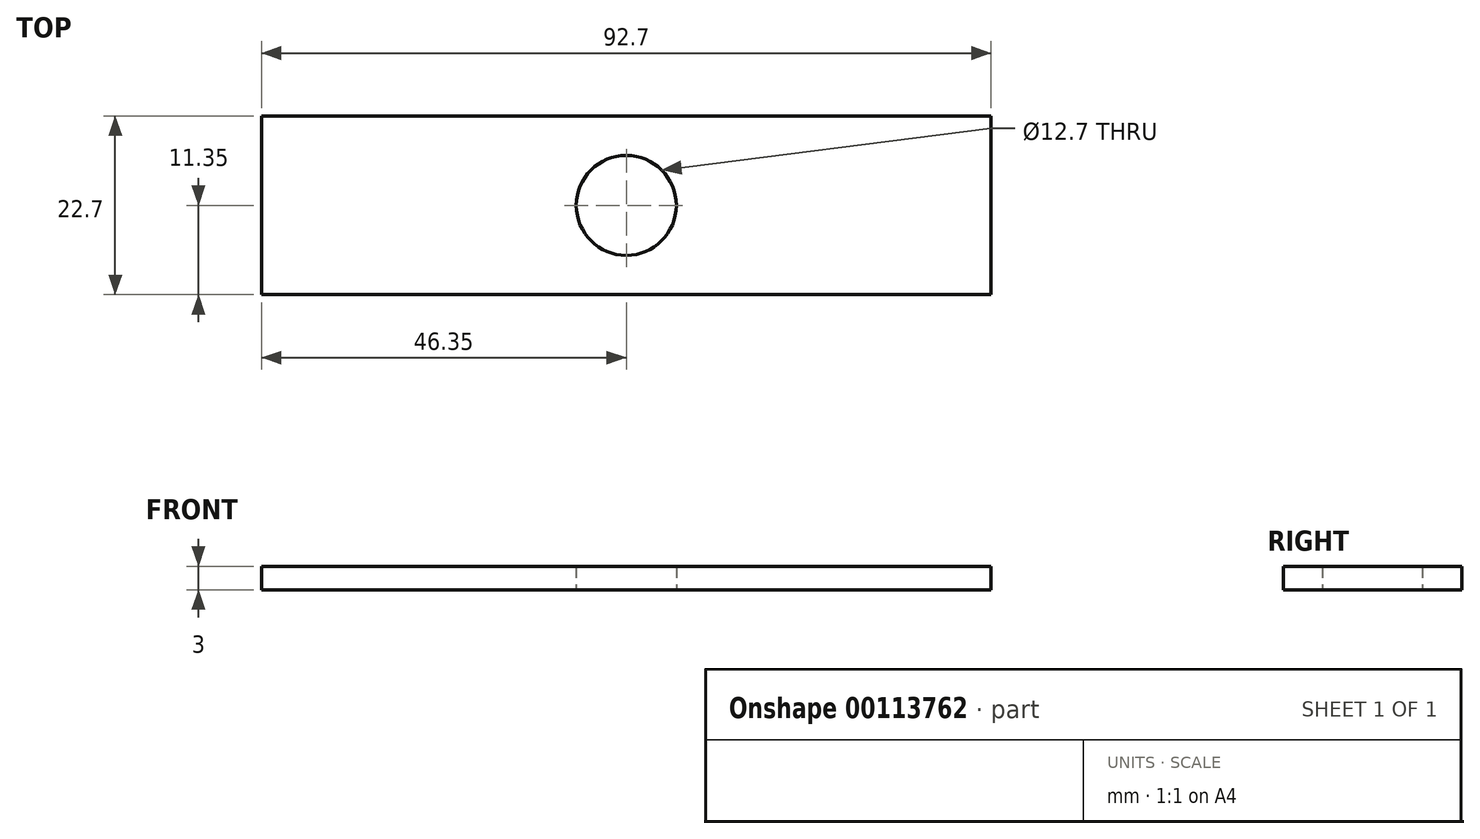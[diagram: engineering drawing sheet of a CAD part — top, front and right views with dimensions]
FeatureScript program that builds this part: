
annotation { "Feature Type Name" : "Feature", "Feature Type Description" : "" }
export const myFeature = defineFeature(function(context is Context, id is Id, definition is map)
    precondition{}
    {
        {
            var Q0;
            Q0=qCreatedBy(makeId("Top.planeOp"),FACE);
            var sketch = newSketch(context, id + "F0", { "sketchPlane" : qUnion([Q0])});
            skLineSegment(sketch, "E0.bottom", {"start": v(46.35, -11.35) * mm, "end": v(-46.35, -11.35) * mm});
            skLineSegment(sketch, "E0.top", {"start": v(46.35, 11.35) * mm, "end": v(-46.35, 11.35) * mm});
            skLineSegment(sketch, "E0.left", {"start": v(46.35, -11.35) * mm, "end": v(46.35, 11.35) * mm});
            skLineSegment(sketch, "E0.right", {"start": v(-46.35, -11.35) * mm, "end": v(-46.35, 11.35) * mm});
            skPoint(sketch, "E0.middle", {"position": v(0, 0) * mm});
            skCircle(sketch, "E1", {"center": v(0, 0) * mm, "radius": 6.35 * mm});
            skLineSegment(sketch, "E2", {"start": v(0, -11.35) * mm, "end": v(0, 11.35) * mm, "construction": true});
            skSolve(sketch);
        }
        {
            var Q0;
            Q0=makeQuery(id+"F0.imprint","IMPRINT",FACE,{"disambiguationData":[TD([[makeQuery(id+"F0.imprint","IMPRINT",EDGE,{"derivedFrom":sQuery(id+"F0.wireOp",EDGE,"E0.bottom")}),-1.0]])]});
            extrude(context, id + "F1", {"entities" : qUnion([Q0]), "depth" : 3 * mm});
        }
    });
